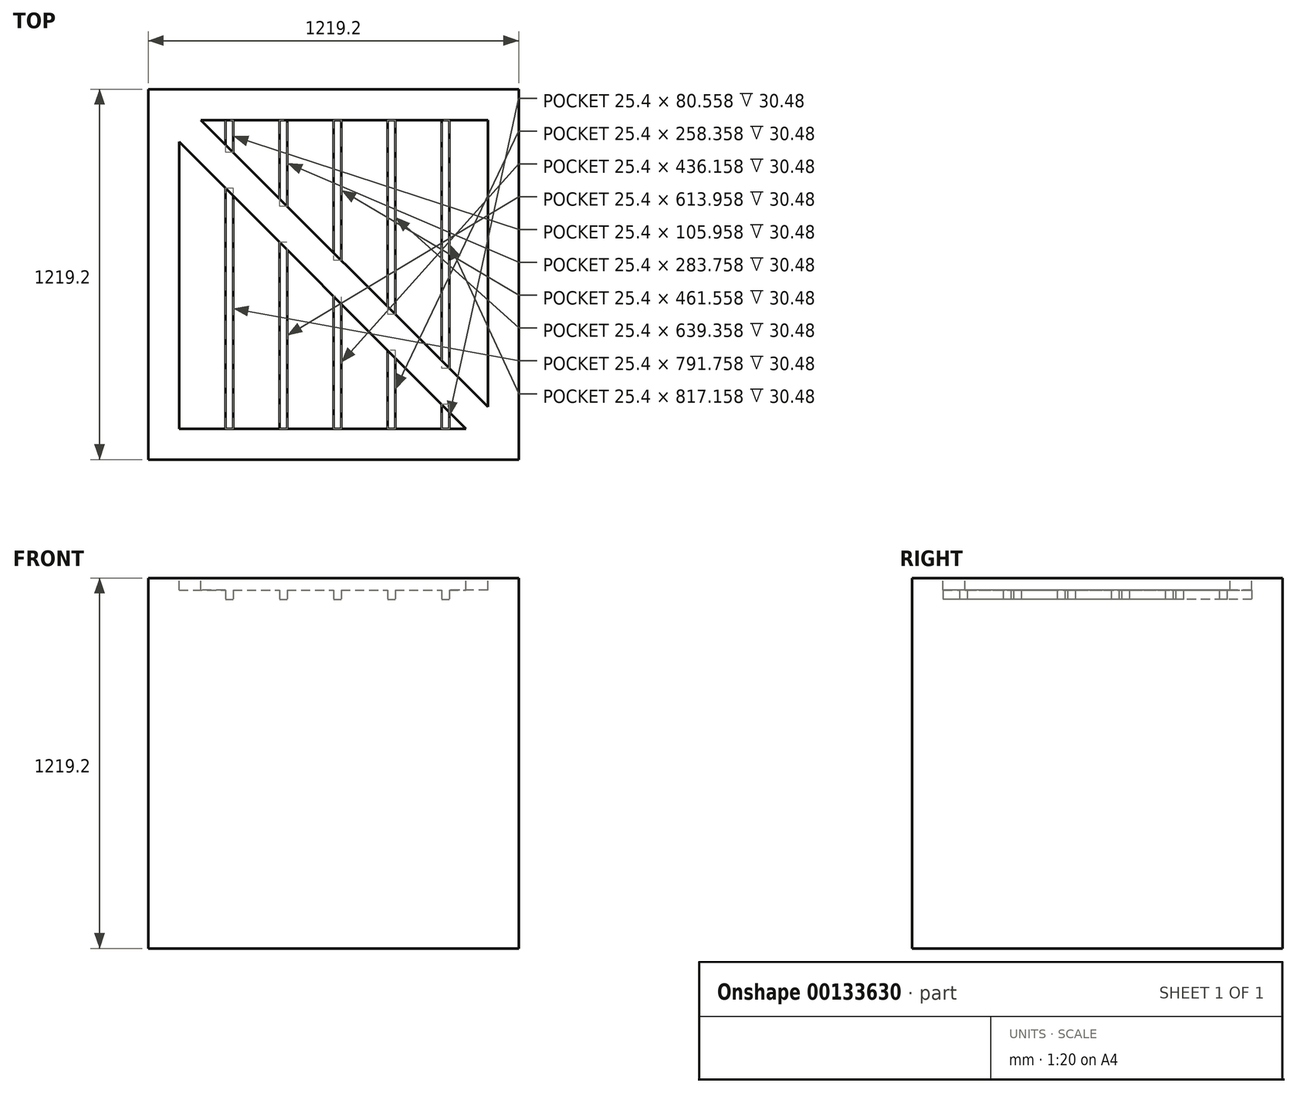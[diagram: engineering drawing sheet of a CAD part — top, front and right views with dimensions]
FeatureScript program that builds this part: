
annotation { "Feature Type Name" : "Feature", "Feature Type Description" : "" }
export const myFeature = defineFeature(function(context is Context, id is Id, definition is map)
    precondition{}
    {
        {
            var Q0;
            Q0=qCreatedBy(makeId("Top.planeOp"),FACE);
            var sketch = newSketch(context, id + "F0", { "sketchPlane" : qUnion([Q0])});
            skLineSegment(sketch, "E0.bottom", {"start": v(609.6, 609.6) * mm, "end": v(-609.6, 609.6) * mm});
            skLineSegment(sketch, "E0.top", {"start": v(609.6, -609.6) * mm, "end": v(-609.6, -609.6) * mm});
            skLineSegment(sketch, "E0.left", {"start": v(609.6, 609.6) * mm, "end": v(609.6, -609.6) * mm});
            skLineSegment(sketch, "E0.right", {"start": v(-609.6, 609.6) * mm, "end": v(-609.6, -609.6) * mm});
            skPoint(sketch, "E0.middle", {"position": v(0, 0) * mm});
            skSolve(sketch);
        }
        {
            var Q0;
            Q0 = qSketchRegion(id + "F0", true);
            extrude(context, id + "F1", {"entities" : qUnion([Q0]), "depth" : 1219.2 * mm});
        }
        {
            var Q0;
            Q0=makeQuery(id+"F1.opExtrude","CAP_FACE",FACE,{"disambiguationData":[OSD([sQuery(id+"F0.wireOp",EDGE,"E0.bottom"),sQuery(id+"F0.wireOp",EDGE,"E0.top"),sQuery(id+"F0.wireOp",EDGE,"E0.left"),sQuery(id+"F0.wireOp",EDGE,"E0.right")])],"isStart":false});
            var sketch = newSketch(context, id + "F2", { "sketchPlane" : qUnion([Q0])});
            skLineSegment(sketch, "E1.0", {"start": v(508, -508) * mm, "end": v(508, 508) * mm});
            skLineSegment(sketch, "E1.1", {"start": v(-508, -508) * mm, "end": v(508, -508) * mm});
            skLineSegment(sketch, "E1.2", {"start": v(-508, 508) * mm, "end": v(-508, -508) * mm});
            skLineSegment(sketch, "E1.3", {"start": v(508, 508) * mm, "end": v(-508, 508) * mm});
            skSolve(sketch);
        }
        {
            var Q0;
            Q0 = qSketchRegion(id + "F2", true);
            extrude(context, id + "F3", {"entities" : qUnion([Q0]), "operationType" : NewBodyOperationType.REMOVE, "oppositeDirection" : true, "depth" : 69.85 * mm});
        }
        {
            var Q0;
            Q0=makeQuery(id+"F1.opExtrude","CAP_FACE",FACE,{"disambiguationData":[OSD([sQuery(id+"F0.wireOp",EDGE,"E0.bottom"),sQuery(id+"F0.wireOp",EDGE,"E0.top"),sQuery(id+"F0.wireOp",EDGE,"E0.left"),sQuery(id+"F0.wireOp",EDGE,"E0.right")])],"isStart":false});
            var sketch = newSketch(context, id + "F4", { "sketchPlane" : qUnion([Q0])});
            skLineSegment(sketch, "E2", {"start": v(-436.16, 508) * mm, "end": v(508, -436.16) * mm});
            skLineSegment(sketch, "E3", {"start": v(-508, 436.16) * mm, "end": v(436.16, -508) * mm});
            skLineSegment(sketch, "E4", {"start": v(-436.16, 508) * mm, "end": v(-508, 508) * mm});
            skLineSegment(sketch, "E5", {"start": v(-508, 508) * mm, "end": v(-508, 436.16) * mm});
            skLineSegment(sketch, "E6", {"start": v(436.16, -508) * mm, "end": v(508, -508) * mm});
            skLineSegment(sketch, "E7", {"start": v(508, -508) * mm, "end": v(508, -436.16) * mm});
            skSolve(sketch);
        }
        {
            var Q0;
            Q0=makeQuery(id+"F4.imprint","IMPRINT",FACE,{"disambiguationData":[TD([[makeQuery(id+"F4.imprint","IMPRINT",EDGE,{"derivedFrom":sQuery(id+"F4.wireOp",EDGE,"E2")}),-1.0]])]});
            extrude(context, id + "F5", {"entities" : qUnion([Q0]), "oppositeDirection" : true, "depth" : 69.85 * mm});
        }
        {
            var Q0;
            Q0=makeQuery(id+"F3.boolean.opBoolean","COPY",FACE,{"derivedFrom":makeQuery(id+"F3.opExtrude","CAP_FACE",FACE,{"disambiguationData":[OSD([sQuery(id+"F2.wireOp",EDGE,"E1.0"),sQuery(id+"F2.wireOp",EDGE,"E1.1"),sQuery(id+"F2.wireOp",EDGE,"E1.2"),sQuery(id+"F2.wireOp",EDGE,"E1.3")])],"isStart":false})});
            var sketch = newSketch(context, id + "F6", { "sketchPlane" : qUnion([Q0])});
            skLineSegment(sketch, "E8.bottom", {"start": v(-508, 508) * mm, "end": v(-355.6, 508) * mm});
            skLineSegment(sketch, "E8.top", {"start": v(-508, -508) * mm, "end": v(-355.6, -508) * mm});
            skLineSegment(sketch, "E8.left", {"start": v(-508, 508) * mm, "end": v(-508, -508) * mm});
            skLineSegment(sketch, "E8.right", {"start": v(-355.6, 508) * mm, "end": v(-355.6, -508) * mm});
            skLineSegment(sketch, "E9.1.0.0", {"start": v(-330.2, 508) * mm, "end": v(-330.2, -508) * mm});
            skLineSegment(sketch, "E9.1.0.1", {"start": v(-177.8, 508) * mm, "end": v(-177.8, -508) * mm});
            skLineSegment(sketch, "E9.2.0.0", {"start": v(-152.4, 508) * mm, "end": v(-152.4, -508) * mm});
            skLineSegment(sketch, "E9.2.0.1", {"start": v(0, 508) * mm, "end": v(0, -508) * mm});
            skLineSegment(sketch, "E9.3.0.0", {"start": v(25.4, 508) * mm, "end": v(25.4, -508) * mm});
            skLineSegment(sketch, "E9.3.0.1", {"start": v(177.8, 508) * mm, "end": v(177.8, -508) * mm});
            skLineSegment(sketch, "E9.4.0.0", {"start": v(203.2, 508) * mm, "end": v(203.2, -508) * mm});
            skLineSegment(sketch, "E9.4.0.1", {"start": v(355.6, 508) * mm, "end": v(355.6, -508) * mm});
            skLineSegment(sketch, "E9.5.0.0", {"start": v(381, 508) * mm, "end": v(381, -508) * mm});
            skLineSegment(sketch, "E9.5.0.1", {"start": v(533.4, 508) * mm, "end": v(533.4, -508) * mm});
            skLineSegment(sketch, "E9.direction1", {"start": v(-508, -508) * mm, "end": v(-330.2, -508) * mm, "construction": true});
            skSolve(sketch);
        }
        {
            var Q0;
            Q0 = qSketchRegion(id + "F6", true);
            var Q1;
            {var subQ0=sQuery(id+"F6.wireOp",EDGE,"E9.1.0.0");Q1=makeQuery(id+"F6.imprint","IMPRINT",FACE,{"disambiguationData":[TD([[makeQuery(id+"F6.imprint","IMPRINT",EDGE,{"derivedFrom":subQ0}),1.0]])]});}
            var Q2;
            {var subQ0=sQuery(id+"F6.wireOp",EDGE,"E9.2.0.0");Q2=makeQuery(id+"F6.imprint","IMPRINT",FACE,{"disambiguationData":[TD([[makeQuery(id+"F6.imprint","IMPRINT",EDGE,{"derivedFrom":subQ0}),1.0]])]});}
            var Q3;
            {var subQ0=sQuery(id+"F6.wireOp",EDGE,"E9.3.0.0");Q3=makeQuery(id+"F6.imprint","IMPRINT",FACE,{"disambiguationData":[TD([[makeQuery(id+"F6.imprint","IMPRINT",EDGE,{"derivedFrom":subQ0}),1.0]])]});}
            var Q4;
            {var subQ0=sQuery(id+"F6.wireOp",EDGE,"E9.4.0.0");Q4=makeQuery(id+"F6.imprint","IMPRINT",FACE,{"disambiguationData":[TD([[makeQuery(id+"F6.imprint","IMPRINT",EDGE,{"derivedFrom":subQ0}),1.0]])]});}
            var Q5;
            {var subQ0=sQuery(id+"F6.wireOp",EDGE,"E9.5.0.0");Q5=makeQuery(id+"F6.imprint","IMPRINT",FACE,{"disambiguationData":[TD([[makeQuery(id+"F6.imprint","IMPRINT",EDGE,{"derivedFrom":subQ0}),1.0]])]});}
            extrude(context, id + "F7", {"entities" : qUnion([Q0, Q1, Q2, Q3, Q4, Q5]), "operationType" : NewBodyOperationType.ADD, "depth" : 30.48 * mm});
        }
        {
            var Q0;
            Q0=makeQuery(id+"F7.boolean.opBoolean","MERGE",FACE,{"derivedFrom":[makeQuery(id+"F1.opExtrude","CAP_FACE",FACE,{"disambiguationData":[OSD([sQuery(id+"F0.wireOp",EDGE,"E0.bottom"),sQuery(id+"F0.wireOp",EDGE,"E0.top"),sQuery(id+"F0.wireOp",EDGE,"E0.left"),sQuery(id+"F0.wireOp",EDGE,"E0.right")])],"isStart":false}),makeQuery(id+"F5.opExtrude","CAP_FACE",FACE,{"disambiguationData":[OSD([sQuery(id+"F4.wireOp",EDGE,"E2"),sQuery(id+"F4.wireOp",EDGE,"E3"),sQuery(id+"F4.wireOp",EDGE,"E4"),sQuery(id+"F4.wireOp",EDGE,"E5"),sQuery(id+"F4.wireOp",EDGE,"E6"),sQuery(id+"F4.wireOp",EDGE,"E7")])],"isStart":true})]});
            cPlane(context, id + "F8", {"entities" : qUnion([Q0]), "cplaneType" : CPlaneType.OFFSET, "offset" : 609.6 * mm, "oppositeDirection" : true, "width" : 152.4 * mm, "height" : 152.4 * mm});
        }
        {
            var Q0;
            Q0=qCreatedBy(id+"F8.planeOp",FACE);
            var sketch = newSketch(context, id + "F9", { "sketchPlane" : qUnion([Q0])});
            skLineSegment(sketch, "E10", {"start": v(0, 0) * mm, "end": v(-960.31, 0) * mm});
            skLineSegment(sketch, "E11", {"start": v(0, 0) * mm, "end": v(0, -833.57) * mm});
            skSolve(sketch);
        }
    });
